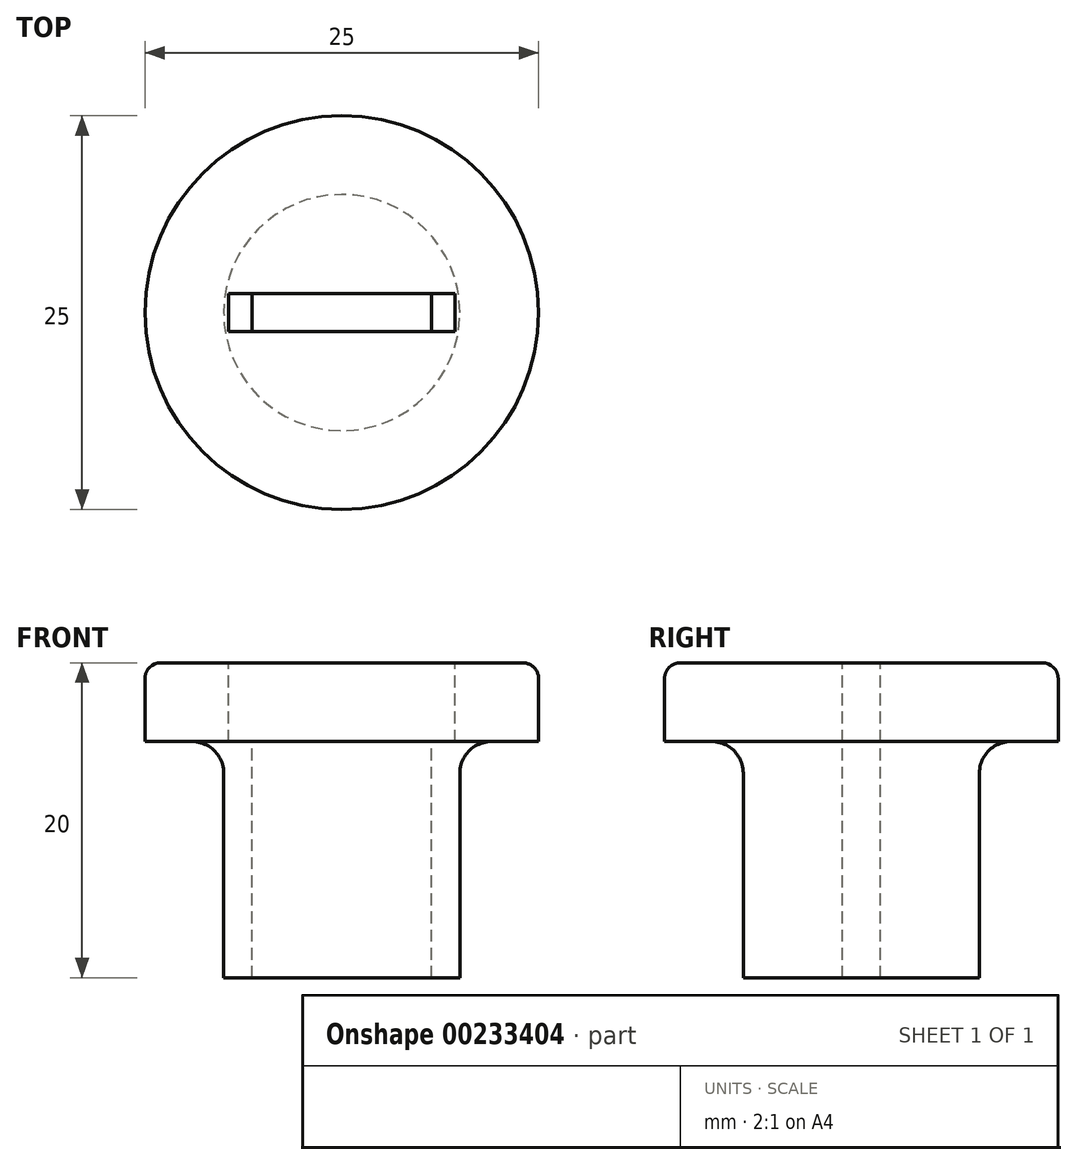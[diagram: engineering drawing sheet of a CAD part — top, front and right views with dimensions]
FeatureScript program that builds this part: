
annotation { "Feature Type Name" : "Feature", "Feature Type Description" : "" }
export const myFeature = defineFeature(function(context is Context, id is Id, definition is map)
    precondition{}
    {
        {
            var Q0;
            Q0=qCreatedBy(makeId("Top.planeOp"),FACE);
            var sketch = newSketch(context, id + "F0", { "sketchPlane" : qUnion([Q0])});
            skPoint(sketch, "E0", {"position": v(0, 0) * mm});
            skCircle(sketch, "E1", {"center": v(0, 0) * mm, "radius": 12.5 * mm});
            skSolve(sketch);
        }
        {
            var Q0;
            Q0=makeQuery(id+"F0.imprint","IMPRINT",FACE,{"disambiguationData":[TD([[makeQuery(id+"F0.imprint","IMPRINT",EDGE,{"derivedFrom":sQuery(id+"F0.wireOp",EDGE,"E1")}),1.0]])]});
            extrude(context, id + "F1", {"entities" : qUnion([Q0]), "depth" : 20 * mm});
        }
        {
            var Q0;
            Q0=makeQuery(id+"F1.opExtrude","CAP_FACE",FACE,{"disambiguationData":[OSD([sQuery(id+"F0.wireOp",EDGE,"E1")])],"isStart":false});
            var sketch = newSketch(context, id + "F2", { "sketchPlane" : qUnion([Q0])});
            skLineSegment(sketch, "E2.bottom", {"start": v(7.2, -1.2) * mm, "end": v(-7.2, -1.2) * mm});
            skLineSegment(sketch, "E2.top", {"start": v(7.2, 1.2) * mm, "end": v(-7.2, 1.2) * mm});
            skLineSegment(sketch, "E2.left", {"start": v(7.2, -1.2) * mm, "end": v(7.2, 1.2) * mm});
            skLineSegment(sketch, "E2.right", {"start": v(-7.2, -1.2) * mm, "end": v(-7.2, 1.2) * mm});
            skPoint(sketch, "E2.middle", {"position": v(0, 0) * mm});
            skSolve(sketch);
        }
        {
            var Q0;
            Q0 = qSketchRegion(id + "F2", true);
            extrude(context, id + "F3", {"entities" : qUnion([Q0]), "operationType" : NewBodyOperationType.REMOVE, "oppositeDirection" : true, "depth" : 5 * mm});
        }
        {
            var Q0;
            Q0=makeQuery(id+"F1.opExtrude","CAP_FACE",FACE,{"disambiguationData":[OSD([sQuery(id+"F0.wireOp",EDGE,"E1")])],"isStart":true});
            var sketch = newSketch(context, id + "F4", { "sketchPlane" : qUnion([Q0])});
            skCircle(sketch, "E3", {"center": v(0, 0) * mm, "radius": 7.5 * mm});
            skSolve(sketch);
        }
        {
            var Q0;
            Q0=makeQuery(id+"F4.imprint","IMPRINT",FACE,{"disambiguationData":[TD([[makeQuery(id+"F4.imprint","IMPRINT",EDGE,{"derivedFrom":sQuery(id+"F4.wireOp",EDGE,"E3")}),-1.0]])]});
            extrude(context, id + "F5", {"entities" : qUnion([Q0]), "operationType" : NewBodyOperationType.REMOVE, "oppositeDirection" : true, "depth" : 15 * mm});
        }
        {
            var Q0;
            Q0=makeQuery(id+"F3.boolean.opBoolean","COPY",FACE,{"derivedFrom":makeQuery(id+"F3.opExtrude","CAP_FACE",FACE,{"disambiguationData":[OSD([sQuery(id+"F2.wireOp",EDGE,"E2.bottom"),sQuery(id+"F2.wireOp",EDGE,"E2.top"),sQuery(id+"F2.wireOp",EDGE,"E2.left"),sQuery(id+"F2.wireOp",EDGE,"E2.right")])],"isStart":false})});
            var sketch = newSketch(context, id + "F6", { "sketchPlane" : qUnion([Q0])});
            skPoint(sketch, "E4", {"position": v(0, 0) * mm});
            skLineSegment(sketch, "E5.bottom", {"start": v(5.7, -1.2) * mm, "end": v(-5.7, -1.2) * mm});
            skLineSegment(sketch, "E5.top", {"start": v(5.7, 1.2) * mm, "end": v(-5.7, 1.2) * mm});
            skLineSegment(sketch, "E5.left", {"start": v(5.7, -1.2) * mm, "end": v(5.7, 1.2) * mm});
            skLineSegment(sketch, "E5.right", {"start": v(-5.7, -1.2) * mm, "end": v(-5.7, 1.2) * mm});
            skSolve(sketch);
        }
        {
            var Q0;
            Q0=makeQuery(id+"F6.imprint","IMPRINT",FACE,{"disambiguationData":[TD([[makeQuery(id+"F6.imprint","IMPRINT",EDGE,{"derivedFrom":sQuery(id+"F6.wireOp",EDGE,"E5.bottom")}),-1.0]])]});
            extrude(context, id + "F7", {"entities" : qUnion([Q0]), "operationType" : NewBodyOperationType.REMOVE, "endBound" : BoundingType.THROUGH_ALL, "oppositeDirection" : true, "depth" : 25 * mm});
        }
        {
            var Q0;
            Q0=makeQuery(id+"F5.boolean.opBoolean","COPY",EDGE,{"derivedFrom":makeQuery(id+"F5.opExtrude","CAP_EDGE",EDGE,{"disambiguationData":[OSD([sQuery(id+"F4.wireOp",EDGE,"E3")])],"isStart":false})});
            fillet(context, id + "F8", {"entities" : qUnion([Q0]), "radius" : 2 * mm, "tangentPropagation" : true, "allowEdgeOverflow" : false});
        }
        {
            var Q0;
            Q0=makeQuery(id+"F1.opExtrude","CAP_EDGE",EDGE,{"disambiguationData":[OSD([sQuery(id+"F0.wireOp",EDGE,"E1")])],"isStart":false});
            var Q1;
            Q1=makeQuery(id+"F5.boolean.opBoolean","COPY",EDGE,{"derivedFrom":makeQuery(id+"F5.opExtrude","CAP_EDGE",EDGE,{"disambiguationData":[OSD([sQuery(id+"F0.wireOp",EDGE,"E1")])],"isStart":false})});
            var Q2;
            Q2=makeQuery(id+"F5.boolean.opBoolean","COPY",EDGE,{"derivedFrom":makeQuery(id+"F5.opExtrude","CAP_EDGE",EDGE,{"disambiguationData":[OSD([sQuery(id+"F4.wireOp",EDGE,"E3")])],"isStart":true})});
            fillet(context, id + "F9", {"entities" : qUnion([Q0, Q1, Q2]), "radius" : 1 * mm, "tangentPropagation" : true, "allowEdgeOverflow" : false});
        }
    });
